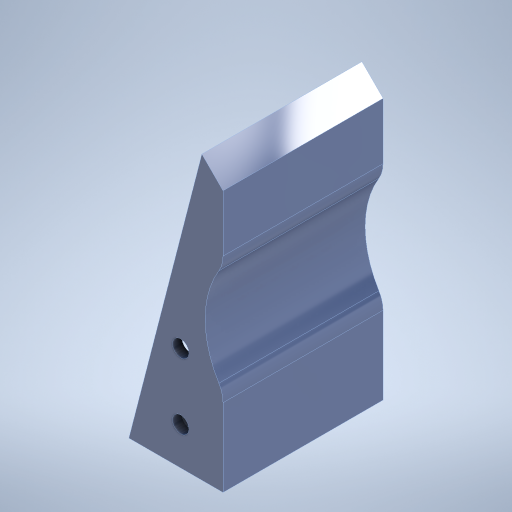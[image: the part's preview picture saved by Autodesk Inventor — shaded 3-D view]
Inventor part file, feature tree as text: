
AUTODESK INVENTOR PART (.ipt)
format: ipt  version: 2024.2 (Build 282272000, 272)  size: 314,880 bytes
history: native  units: mm
features: extrude x6, sketch x6, chamfer x1, fillet x1, shell x1
ambient origin geometry x8: Origin, YZ Plane, XZ Plane, XY Plane, X Axis, Y Axis, Z Axis, Center Point
bodies: Solid1 (feature_tree)
feature tree (15):
  extrude  "Extrusion1"  Depth=20.0mm
  chamfer  "Chamfer1"  Distance=60.0mm
  extrude  "Extrusion2"  Depth=2.0mm TaperAngle=0.0deg
  extrude  "Extrusion3"  Depth=2.0mm TaperAngle=0.0deg
  fillet  "Fillet1"  Radius=6.0mm
  shell  "Shell1"  Thickness=2.0mm
  extrude  "Extrusion4"  Depth=30.0mm
  extrude  "Extrusion5"  Depth=34.0mm TaperAngle=0.0deg
  extrude  "Extrusion6"  Depth=10.0mm
  sketch  "Sketch1"  dims[d0=34.0mm d1=20.0mm d2=60.0mm d3=0.0mm]
  sketch  "Sketch3"  dims[d4=4.5mm d5=2.0mm d6=45.0deg d7=60.0mm d8=0.0mm]
  sketch  "Sketch4"  dims[d9=39.6mm d10=60.0mm d11=0.0mm d12=6.0mm d13=2.0mm]
  sketch  "Sketch5"  dims[d14=16.0mm d15=30.0mm]
  sketch  "Sketch6"  dims[d16=3.0mm d17=34.0mm d18=0.0mm]
  sketch  "Sketch7"  dims[d19=4.5mm d20=4.5mm d21=5.0mm d22=20.0mm d24=10.0mm d25=20.0mm d27=25.0mm d30=3.0mm d31=0.0mm d32=3.5mm d33=8.0mm d34=11.0mm d35=20.0mm d37=14.0mm d38=10.0mm d40=10.0mm d42=0.0mm d43=0.0mm]
